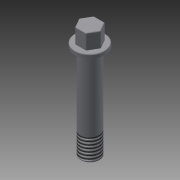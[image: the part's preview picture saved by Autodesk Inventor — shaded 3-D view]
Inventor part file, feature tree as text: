
AUTODESK INVENTOR PART (.ipt)
format: ipt  version: 2015 (Build 190159000, 159)  size: 123,904 bytes
history: native  units: mm
features: extrude x3, sketch x3, thread x1, chamfer x1, fillet x1
ambient origin geometry x8: Origin, YZ Plane, XZ Plane, XY Plane, X Axis, Y Axis, Z Axis, Center Point
bodies: 实体1 (feature_tree)
feature tree (9):
  extrude  "拉伸1"  Depth=1.0mm TaperAngle=0.0deg
  extrude  "拉伸2"  Depth=5.0mm
  extrude  "拉伸3"  Depth=5.0mm
  thread  "螺纹1"  [1 undecoded]
  chamfer  "倒角1"  Distance=6.0mm
  fillet  "圆角1"  Radius=0.25mm
  sketch  "草图1"  dims[d0=8.0mm d1=1.0mm d2=0.0mm]
  sketch  "草图2"  dims[d3=1.506698mm d4=5.0mm]
  sketch  "草图3"  dims[d5=4.0mm d6=0.0mm d7=5.0mm d8=25.0mm d9=0.0mm d10=6.0mm d11=0.0mm d12=0.25mm d13=2.0mm d14=45.0deg d15=0.25mm]
note: 1 required parameter value undecoded (feature->parameter linkage not recoverable at this tier; creation-order binding heuristic only, values carry confidence <= 0.55)
